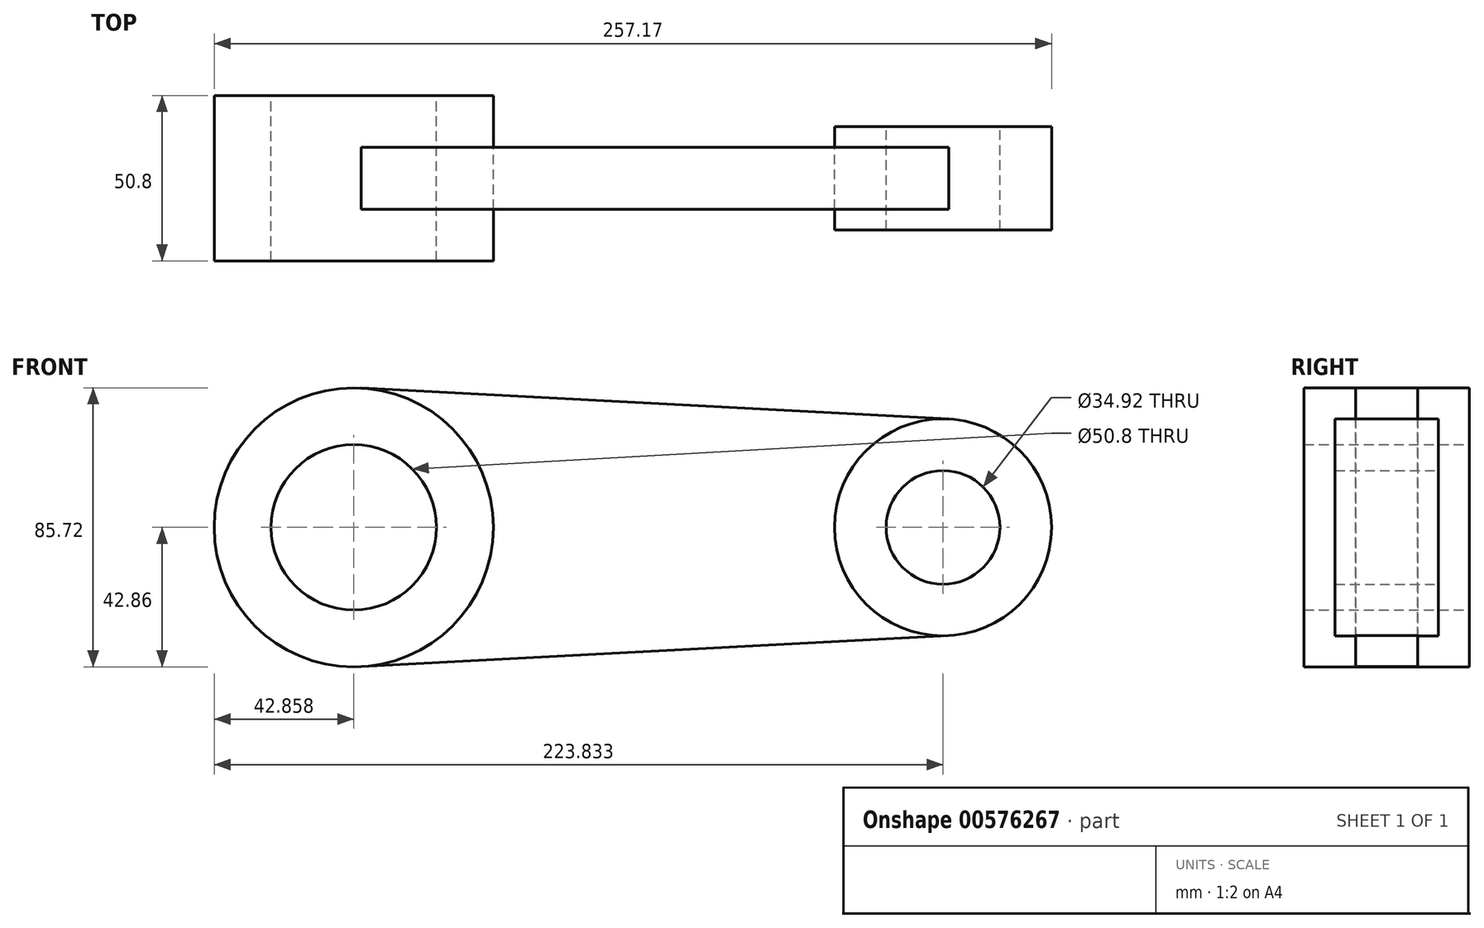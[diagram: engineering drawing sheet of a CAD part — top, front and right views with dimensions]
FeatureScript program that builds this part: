
annotation { "Feature Type Name" : "Feature", "Feature Type Description" : "" }
export const myFeature = defineFeature(function(context is Context, id is Id, definition is map)
    precondition{}
    {
        {
            var Q0;
            Q0=qCreatedBy(makeId("Front.planeOp"),FACE);
            var sketch = newSketch(context, id + "F0", { "sketchPlane" : qUnion([Q0])});
            skLineSegment(sketch, "E0", {"start": v(-42.9, 0) * mm, "end": v(138.07, 0) * mm});
            skCircle(sketch, "E1", {"center": v(-42.9, 0) * mm, "radius": 42.86 * mm});
            skCircle(sketch, "E2", {"center": v(-42.9, 0) * mm, "radius": 25.4 * mm});
            skCircle(sketch, "E3", {"center": v(138.07, 0) * mm, "radius": 33.34 * mm});
            skCircle(sketch, "E4", {"center": v(138.07, 0) * mm, "radius": 17.46 * mm});
            skLineSegment(sketch, "E5", {"start": v(-40.65, 42.8) * mm, "end": v(139.83, 33.3) * mm});
            skLineSegment(sketch, "E6", {"start": v(-40.65, -42.8) * mm, "end": v(139.83, -33.3) * mm});
            skSolve(sketch);
        }
        {
            var Q0;
            Q0=makeQuery(id+"F0.imprint","IMPRINT",FACE,{"disambiguationData":[TD([[makeQuery(id+"F0.imprint","IMPRINT",EDGE,{"derivedFrom":sQuery(id+"F0.wireOp",EDGE,"E2")}),-1.0]])]});
            extrude(context, id + "F1", {"entities" : qUnion([Q0]), "endBound" : BoundingType.SYMMETRIC, "depth" : 50.8 * mm, "offsetDistance" : 25.4 * mm});
        }
        {
            var Q0;
            Q0=makeQuery(id+"F0.imprint","IMPRINT",FACE,{"disambiguationData":[TD([[makeQuery(id+"F0.imprint","IMPRINT",EDGE,{"derivedFrom":sQuery(id+"F0.wireOp",EDGE,"E4")}),-1.0]])]});
            extrude(context, id + "F2", {"entities" : qUnion([Q0]), "endBound" : BoundingType.SYMMETRIC, "depth" : 31.75 * mm, "offsetDistance" : 25.4 * mm});
        }
        {
            var Q0;
            {var subQ5=sQuery(id+"F0.wireOp",EDGE,"E5");Q0=makeQuery(id+"F0.imprint","IMPRINT",FACE,{"disambiguationData":[TD([[makeQuery(id+"F0.imprint","IMPRINT",EDGE,{"derivedFrom":subQ5}),-1.0]])]});}
            var Q1;
            {var subQ5=sQuery(id+"F0.wireOp",EDGE,"E6");Q1=makeQuery(id+"F0.imprint","IMPRINT",FACE,{"disambiguationData":[TD([[makeQuery(id+"F0.imprint","IMPRINT",EDGE,{"derivedFrom":subQ5}),1.0]])]});}
            extrude(context, id + "F3", {"entities" : qUnion([Q0, Q1]), "endBound" : BoundingType.SYMMETRIC, "depth" : 19.05 * mm, "offsetDistance" : 25.4 * mm});
        }
    });
